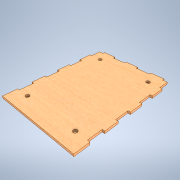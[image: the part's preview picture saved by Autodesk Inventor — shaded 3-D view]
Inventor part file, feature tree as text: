
AUTODESK INVENTOR PART (.ipt)
format: ipt  version: 2021 (Build 250183000, 183)  size: 214,016 bytes
history: native  units: mm
features: extrude x3, sketch x2, other x1
ambient origin geometry x8: Origin, YZ Plane, XZ Plane, XY Plane, X Axis, Y Axis, Z Axis, Center Point
bodies: Body1 (feature_tree)
feature tree (6):
  other  "DoosjeOnderkant"
  extrude  "Extrusion2"  Depth=140.0mm
  extrude  "Extrusion3"  Depth=3.0mm TaperAngle=0.0deg
  extrude  "Extrusion4"  Depth=2.5mm TaperAngle=0.0deg
  sketch  "Sketch3"  dims[d4=105.0mm d5=140.0mm]
  sketch  "Sketch5"  dims[d6=3.0mm d7=0.0mm d29=3.0mm d30=0.0mm d41=2.5mm d42=0.0mm d51=3.0mm d52=17.5mm d53=17.5mm d54=17.5mm d55=17.5mm d56=17.5mm d58=3.0mm d65=17.5mm d66=17.5mm d67=17.5mm d69=5.75mm d70=5.75mm d71=17.5mm d72=17.5mm d73=20.0mm d75=70.0mm d76=20.0mm d78=105.0mm d2=0.5mm d3=0.872665mm]
